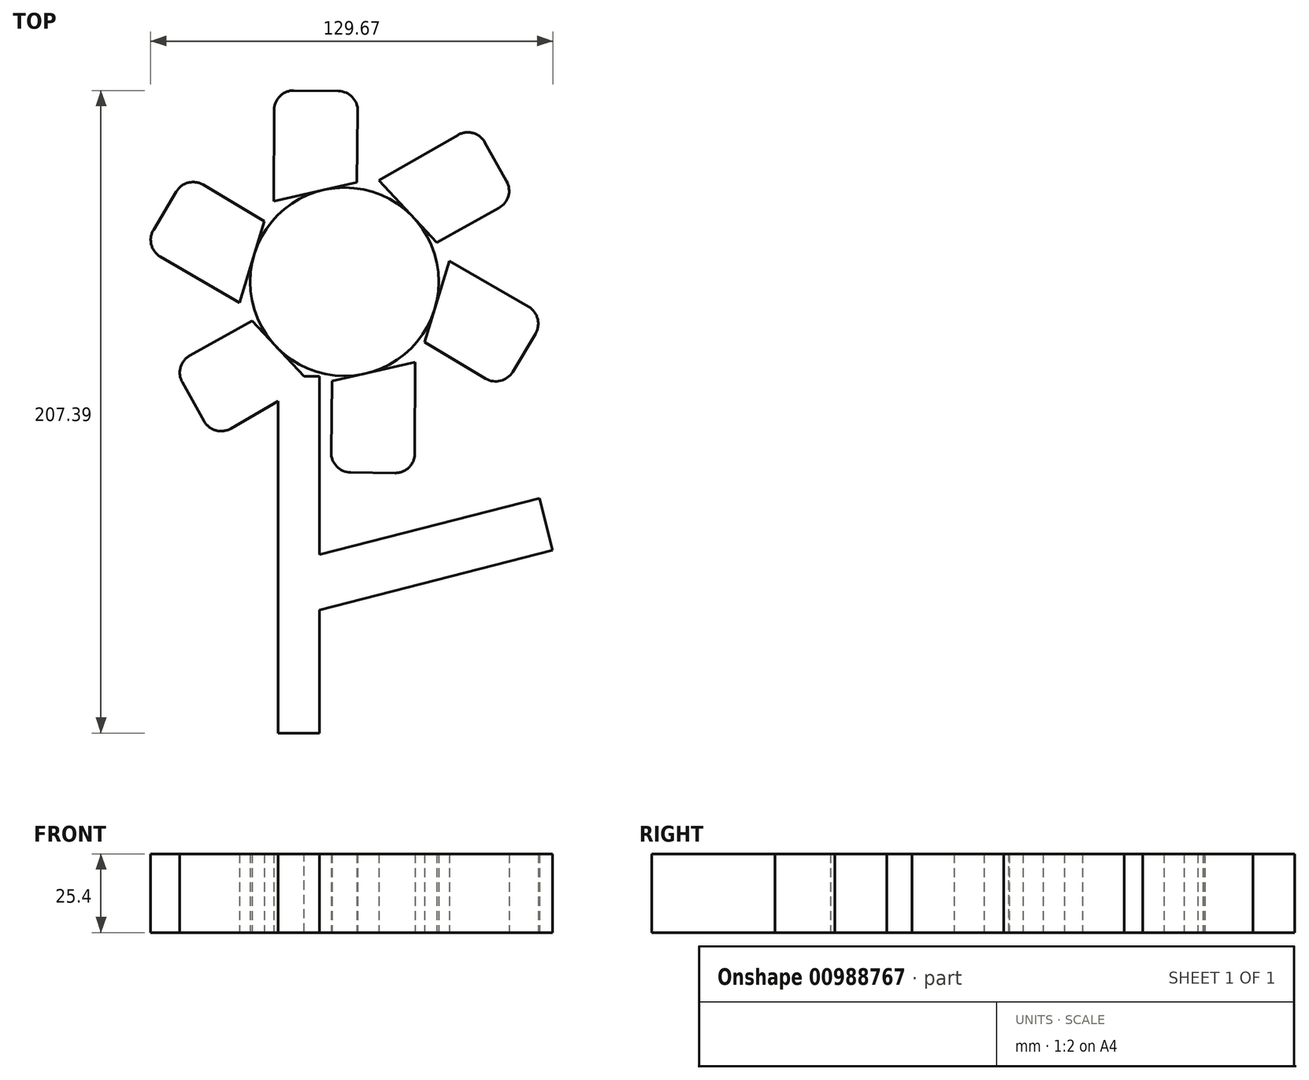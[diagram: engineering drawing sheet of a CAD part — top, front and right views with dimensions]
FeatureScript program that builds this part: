
annotation { "Feature Type Name" : "Feature", "Feature Type Description" : "" }
export const myFeature = defineFeature(function(context is Context, id is Id, definition is map)
    precondition{}
    {
        {
            var Q0;
            Q0=qCreatedBy(makeId("Top.planeOp"),FACE);
            var sketch = newSketch(context, id + "F0", { "sketchPlane" : qUnion([Q0])});
            skCircle(sketch, "E0", {"center": v(0, 0) * mm, "radius": 30.4 * mm});
            skLineSegment(sketch, "E1", {"start": v(11.08, 32.67) * mm, "end": v(29.8, 12.61) * mm});
            skLineSegment(sketch, "E2", {"start": v(29.8, 12.61) * mm, "end": v(49.86, 23.81) * mm});
            skLineSegment(sketch, "E3", {"start": v(52.3, 32.45) * mm, "end": v(45.32, 44.96) * mm});
            skLineSegment(sketch, "E4", {"start": v(36.6, 47.37) * mm, "end": v(11.08, 32.67) * mm});
            skPoint(sketch, "E5.visualSharp", {"position": v(42.18, 50.58) * mm});
            skArc(sketch, "E5.filletArc", {"start": v(45.32, 44.96) * mm, "mid": v(41.47, 47.99) * mm, "end": v(36.6, 47.37) * mm});
            skPoint(sketch, "E6.visualSharp", {"position": v(55.4, 26.9) * mm});
            skArc(sketch, "E6.filletArc", {"start": v(49.86, 23.81) * mm, "mid": v(52.87, 27.63) * mm, "end": v(52.3, 32.45) * mm});
            skLineSegment(sketch, "E7.1.0", {"start": v(-22.72, 55.39) * mm, "end": v(-22.75, 25.93) * mm});
            skArc(sketch, "E7.1.1", {"start": v(-16.28, 61.73) * mm, "mid": v(-20.82, 59.9) * mm, "end": v(-22.72, 55.39) * mm});
            skLineSegment(sketch, "E7.1.2", {"start": v(-1.95, 61.53) * mm, "end": v(-16.28, 61.73) * mm});
            skArc(sketch, "E7.1.3", {"start": v(4.3, 55.09) * mm, "mid": v(2.51, 59.6) * mm, "end": v(-1.95, 61.53) * mm});
            skLineSegment(sketch, "E7.1.4", {"start": v(3.98, 32.12) * mm, "end": v(4.3, 55.09) * mm});
            skLineSegment(sketch, "E7.1.5", {"start": v(-22.75, 25.93) * mm, "end": v(3.98, 32.12) * mm});
            skLineSegment(sketch, "E7.2.0", {"start": v(-59.32, 8.02) * mm, "end": v(-33.83, -6.74) * mm});
            skArc(sketch, "E7.2.1", {"start": v(-61.6, 16.77) * mm, "mid": v(-62.3, 11.92) * mm, "end": v(-59.32, 8.02) * mm});
            skLineSegment(sketch, "E7.2.2", {"start": v(-54.26, 29.07) * mm, "end": v(-61.6, 16.77) * mm});
            skArc(sketch, "E7.2.3", {"start": v(-45.55, 31.27) * mm, "mid": v(-50.36, 31.98) * mm, "end": v(-54.26, 29.07) * mm});
            skLineSegment(sketch, "E7.2.4", {"start": v(-25.82, 19.5) * mm, "end": v(-45.55, 31.27) * mm});
            skLineSegment(sketch, "E7.2.5", {"start": v(-33.83, -6.74) * mm, "end": v(-25.82, 19.5) * mm});
            skLineSegment(sketch, "E7.3.0", {"start": v(-36.6, -47.37) * mm, "end": v(-11.08, -32.67) * mm});
            skArc(sketch, "E7.3.1", {"start": v(-45.32, -44.96) * mm, "mid": v(-41.47, -47.99) * mm, "end": v(-36.6, -47.37) * mm});
            skLineSegment(sketch, "E7.3.2", {"start": v(-52.3, -32.45) * mm, "end": v(-45.32, -44.96) * mm});
            skArc(sketch, "E7.3.3", {"start": v(-49.86, -23.81) * mm, "mid": v(-52.87, -27.63) * mm, "end": v(-52.3, -32.45) * mm});
            skLineSegment(sketch, "E7.3.4", {"start": v(-29.8, -12.61) * mm, "end": v(-49.86, -23.81) * mm});
            skLineSegment(sketch, "E7.3.5", {"start": v(-11.08, -32.67) * mm, "end": v(-29.8, -12.61) * mm});
            skLineSegment(sketch, "E7.4.0", {"start": v(22.72, -55.39) * mm, "end": v(22.75, -25.93) * mm});
            skArc(sketch, "E7.4.1", {"start": v(16.28, -61.73) * mm, "mid": v(20.82, -59.9) * mm, "end": v(22.72, -55.39) * mm});
            skLineSegment(sketch, "E7.4.2", {"start": v(1.95, -61.53) * mm, "end": v(16.28, -61.73) * mm});
            skArc(sketch, "E7.4.3", {"start": v(-4.3, -55.09) * mm, "mid": v(-2.51, -59.6) * mm, "end": v(1.95, -61.53) * mm});
            skLineSegment(sketch, "E7.4.4", {"start": v(-3.98, -32.12) * mm, "end": v(-4.3, -55.09) * mm});
            skLineSegment(sketch, "E7.4.5", {"start": v(22.75, -25.93) * mm, "end": v(-3.98, -32.12) * mm});
            skLineSegment(sketch, "E7.5.0", {"start": v(59.32, -8.02) * mm, "end": v(33.83, 6.74) * mm});
            skArc(sketch, "E7.5.1", {"start": v(61.6, -16.77) * mm, "mid": v(62.3, -11.92) * mm, "end": v(59.32, -8.02) * mm});
            skLineSegment(sketch, "E7.5.2", {"start": v(54.26, -29.07) * mm, "end": v(61.6, -16.77) * mm});
            skArc(sketch, "E7.5.3", {"start": v(45.55, -31.27) * mm, "mid": v(50.36, -31.98) * mm, "end": v(54.26, -29.07) * mm});
            skLineSegment(sketch, "E7.5.4", {"start": v(25.82, -19.5) * mm, "end": v(45.55, -31.27) * mm});
            skLineSegment(sketch, "E7.5.5", {"start": v(33.83, 6.74) * mm, "end": v(25.82, -19.5) * mm});
            skSolve(sketch);
        }
        {
            var Q0;
            {var subQ0=sQuery(id+"F0.wireOp",EDGE,"E0");var subQ4=makeQuery(id+"F0.imprint","INTERSECT",VERTEX,{"derivedFrom":[subQ0,sQuery(id+"F0.wireOp",EDGE,"E7.1.5")]});Q0=makeQuery(id+"F0.imprint","IMPRINT",FACE,{"disambiguationData":[TD([[makeQuery(id+"F0.imprint","IMPRINT",EDGE,{"disambiguationData":[TD([[subQ4,1.0]])],"derivedFrom":subQ0}),1.0]])]});}
            var Q1;
            {var subQ0=sQuery(id+"F0.wireOp",EDGE,"E7.1.0");Q1=makeQuery(id+"F0.imprint","IMPRINT",FACE,{"disambiguationData":[TD([[makeQuery(id+"F0.imprint","IMPRINT",EDGE,{"derivedFrom":subQ0}),1.0]])]});}
            var Q2;
            {var subQ0=sQuery(id+"F0.wireOp",EDGE,"E2");Q2=makeQuery(id+"F0.imprint","IMPRINT",FACE,{"disambiguationData":[TD([[makeQuery(id+"F0.imprint","IMPRINT",EDGE,{"derivedFrom":subQ0}),1.0]])]});}
            var Q3;
            {var subQ0=sQuery(id+"F0.wireOp",EDGE,"E7.5.0");Q3=makeQuery(id+"F0.imprint","IMPRINT",FACE,{"disambiguationData":[TD([[makeQuery(id+"F0.imprint","IMPRINT",EDGE,{"derivedFrom":subQ0}),1.0]])]});}
            var Q4;
            {var subQ0=sQuery(id+"F0.wireOp",EDGE,"E7.4.0");Q4=makeQuery(id+"F0.imprint","IMPRINT",FACE,{"disambiguationData":[TD([[makeQuery(id+"F0.imprint","IMPRINT",EDGE,{"derivedFrom":subQ0}),1.0]])]});}
            var Q5;
            {var subQ0=sQuery(id+"F0.wireOp",EDGE,"E7.3.0");Q5=makeQuery(id+"F0.imprint","IMPRINT",FACE,{"disambiguationData":[TD([[makeQuery(id+"F0.imprint","IMPRINT",EDGE,{"derivedFrom":subQ0}),1.0]])]});}
            var Q6;
            {var subQ0=sQuery(id+"F0.wireOp",EDGE,"E7.2.0");Q6=makeQuery(id+"F0.imprint","IMPRINT",FACE,{"disambiguationData":[TD([[makeQuery(id+"F0.imprint","IMPRINT",EDGE,{"derivedFrom":subQ0}),1.0]])]});}
            extrude(context, id + "F1", {"entities" : qUnion([Q0, Q1, Q2, Q3, Q4, Q5, Q6]), "depth" : 25.4 * mm, "offsetDistance" : 25.4 * mm});
        }
        {
            var Q0;
            Q0=qCreatedBy(makeId("Top.planeOp"),FACE);
            var sketch = newSketch(context, id + "F2", { "sketchPlane" : qUnion([Q0])});
            skLineSegment(sketch, "E8.bottom", {"start": v(-8.03, -30.53) * mm, "end": v(-21.36, -30.53) * mm});
            skLineSegment(sketch, "E8.top", {"start": v(-8.03, -145.66) * mm, "end": v(-21.36, -145.66) * mm});
            skLineSegment(sketch, "E8.left", {"start": v(-8.03, -30.53) * mm, "end": v(-8.03, -145.66) * mm});
            skLineSegment(sketch, "E8.right", {"start": v(-21.36, -30.53) * mm, "end": v(-21.36, -145.66) * mm});
            skLineSegment(sketch, "E9", {"start": v(-8.03, -88.1) * mm, "end": v(62.87, -69.92) * mm});
            skLineSegment(sketch, "E10", {"start": v(62.87, -69.92) * mm, "end": v(67.18, -86.71) * mm});
            skLineSegment(sketch, "E11", {"start": v(67.18, -86.71) * mm, "end": v(-8.03, -106) * mm});
            skSolve(sketch);
        }
        {
            var Q0;
            Q0 = qSketchRegion(id + "F2", true);
            extrude(context, id + "F3", {"entities" : qUnion([Q0]), "operationType" : NewBodyOperationType.ADD, "depth" : 25.4 * mm, "offsetDistance" : 25.4 * mm});
        }
    });
